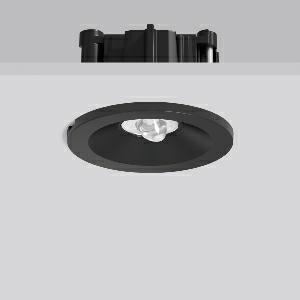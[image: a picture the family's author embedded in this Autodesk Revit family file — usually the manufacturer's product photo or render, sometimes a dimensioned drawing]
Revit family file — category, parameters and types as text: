
# Revit family: turia_l_672561_003_e900
name_source: partatom
category: Lighting Fixtures
units: mm (PartAtom-declared; Revit-internal decimal feet)

## family parameters
Cut with Voids When Loaded = No
Host = Face
Light Source = No
Part Type = Normal
Room Calculation Point = No
Round Connector Dimension = Use Diameter
Shared = No

## types (1)
- TURIA L (1 x LED Modul 765, 240 lm, 6500)
    Apparent Load = 4 VA
    CIE Flux Codes = 70 91 99 100 100
    Color Rendering = 70
    Color Temperature = 6500
    Default Elevation = 1800 mm
    Description = Series: TURIA L
Round emergency luminaire for escape route lighting. Housing: die-cast aluminium. Bezel ring: plastic. With asymmetrical beam plastic lenses for illuminating rescue facilities. Einzelbatteriesystem mit automatischem Selbsttest. With enclosed separate ceiling mounting ring also suitable for ceiling cut-outs of Ø 68 mm. 
Colour: black
Diameter: 62 mm
Height: 3 mm
Cut-out diameter: 54-68 mm
Recess height: 76-162 mm
Luminaire: recess height: 42 mm
Weight: 420 g
Operating mode: non-maintained power mode
Duration time: 3 h
Lamp: LED
Socket: without socket
Colour temperature: 6500K
Colour rendering index (CRI): 70
System power: 4.2 W
Rated luminous flux: 240 lm
Luminous flux, emergency: 170 lm
System power, emergency: -
Control gear: Regulated power supply
Protection class: II
Type of protection: IP 20
    Height = 0 mm  [stored 0 ft]
    Lamp = 1 x LED Modul 765
    Lamp Light Flux = 240 lm
    Lamp count = 1
    Length = 62 mm  [stored 0.203412 ft]
    Lifetime = 50000 h
    Luminous efficacy = 57 lm/W
    Manufacturer = RZB
    ModVariant = No
    Model = 672561.003
    Mounting Place = Ceiling
    Mounting Type = Recessed
    Number of Poles = 1
    OnlyDefault = Yes
    Power Factor = 1
    Product Name = TURIA L
    Product group = Recessed ceiling luminaires
    ProductGroupID = 405
    Protection Class = Protection class II
    Protection Degree = IP 20
    RLX_Detail_Level = 1
    RLX_Emergency_Light_Flux = 170 lm
    RLX_Emergency_Type = 3
    RLX_Emergency_Type_DB = Yes
    RlxData = <blob elided: 58021 chars, md5=55da9629>
    Socket = socket
    Standby Power = 0 W
    System Light Flux = 240 lm
    System Power = 4 W
    Type Comments = Product without accessories
    Type Image = 672561.003.jpg
    URL = http://relux.com
    VarID = ---
    Voltage = 230 V
    Voltage Range = 220-240 V
    Weight = 0.00 kg
    Width = 0 mm  [stored 0 ft]

note: [stored X ft] marks values corroborated as IEEE doubles in the binary element streams (Revit-internal decimal feet)

## geometry (parser evidence)
native form markers: Blend x4, Sweep x12
no freeform markers — native parametric forms only
